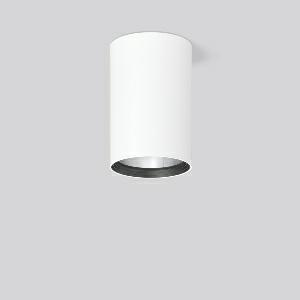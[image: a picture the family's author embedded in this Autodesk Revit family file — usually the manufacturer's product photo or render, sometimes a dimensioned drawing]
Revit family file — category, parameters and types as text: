
# Revit family: heledon_maxi_a_931226_002_76_9bf7
name_source: partatom
category: Lighting Fixtures
units: mm (PartAtom-declared; Revit-internal decimal feet)

## family parameters
Cut with Voids When Loaded = No
Host = Face
Light Source = No
Part Type = Normal
Room Calculation Point = No
Round Connector Dimension = Use Diameter
Shared = No

## types (1)
- HELEDON maxi A (1 x LED Modul 930, 4150 lm, 3000)
    Apparent Load = 35 VA
    Approval mark = CE
    CIE Flux Codes = 97 100 100 100 100
    Color Rendering = 90
    Color Temperature = 3000
    Default Elevation = 1800 mm
    Description = Series: HELEDON maxi
Cylindrical surface-mounted downlight. Housing: die-cast aluminium, powder-coated. Internal ceiling frame polycarbonate with bayonet mounting. Black plastic ring and recessed LED to prevent glare from the side. Optical assembly with reflector made of MIRO-Silver with 98% total light reflection for outstanding efficiency - can be changed without tools. Best colour rendering index Ra>90. Suitable for Ceiling mounting. Easy installation with a separate ceiling frame with bayonet mounting and plug connection. Driver integrated. Connected via plug-in connector. High quality converter without flickering and stroboscopic effect. The following accessories can be mounted without use of tools: interchangeable lenses, decorative glasses, honeycomb louvre, clear and frosted diffusers, white interchangeable plastic ring. 
Colour: traffic white, matt (RAL 9016)
Diameter: 123 mm
Height: 183 mm
Lamp: LED
Socket: without socket
Colour temperature: 3000K
Colour rendering index (CRI): 92
System power: 35 W
Rated luminous flux: 4150 lm
Luminous efficiency: 119 lm/W
Control gear: Converter, dimmable, DALI
Protection class: I
Type of protection: IP 20
    Height = 183 mm
    Lamp = 1 x LED Modul 930
    Lamp Light Flux = 4150 lm
    Lamp count = 1
    Length = 123 mm
    Lifetime = 50000 h
    Luminous efficacy = 119 lm/W
    Manufacturer = RZB
    ModVariant = No
    Model = 931226.002.76
    Mounting Place = Ceiling
    Mounting Type = Surface mounted
    Number of Poles = 1
    OnlyDefault = Yes
    Power Factor = 1
    Product Name = HELEDON maxi A
    Product group = Surface mounted downlights
    ProductGroupID = 302
    Protection Class = Protection class I
    Protection Degree = IP 20
    RLX_Detail_Level = 1
    RLX_Emergency_Light_Flux = 0 lm
    RLX_Emergency_Type = 0
    RLX_Emergency_Type_DB = No
    RlxData = <blob elided: 97941 chars, md5=6e07ec15>
    Socket = socket
    Standby Power = 0 W
    System Light Flux = 4150 lm
    System Power = 35 W
    Type Comments = Product without accessories
    Type Image = 931192.002.jpg
    URL = http://relux.com
    VarID = ---
    Voltage = 230 V
    Voltage Range = 220-240 V
    Weight = 0.00 kg
    Width = 0 mm  [stored 0 ft]

note: [stored X ft] marks values corroborated as IEEE doubles in the binary element streams (Revit-internal decimal feet)

## geometry (parser evidence)
native form markers: Blend x4, Sweep x10
no freeform markers — native parametric forms only
